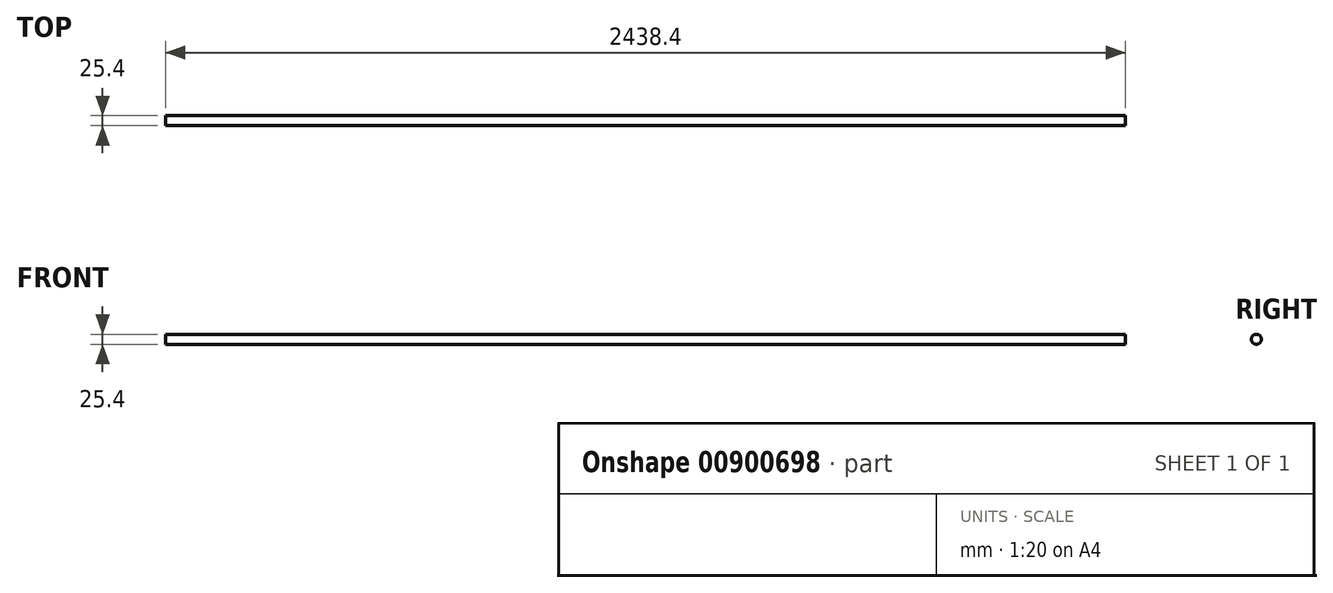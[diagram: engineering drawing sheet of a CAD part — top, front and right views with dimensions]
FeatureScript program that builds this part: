
annotation { "Feature Type Name" : "Feature", "Feature Type Description" : "" }
export const myFeature = defineFeature(function(context is Context, id is Id, definition is map)
    precondition{}
    {
        {
            var Q0;
            Q0=qCreatedBy(makeId("Right.planeOp"),FACE);
            var sketch = newSketch(context, id + "F0", { "sketchPlane" : qUnion([Q0])});
            skCircle(sketch, "E0", {"center": v(0, 0) * mm, "radius": 12.7 * mm});
            skSolve(sketch);
        }
        {
            var Q0;
            Q0=makeQuery(id+"F0.imprint","IMPRINT",FACE,{"disambiguationData":[TD([[makeQuery(id+"F0.imprint","IMPRINT",EDGE,{"derivedFrom":sQuery(id+"F0.wireOp",EDGE,"E0")}),1.0]])]});
            extrude(context, id + "F1", {"entities" : qUnion([Q0]), "depth" : 2438.4 * mm, "offsetDistance" : 25.4 * mm});
        }
    });
